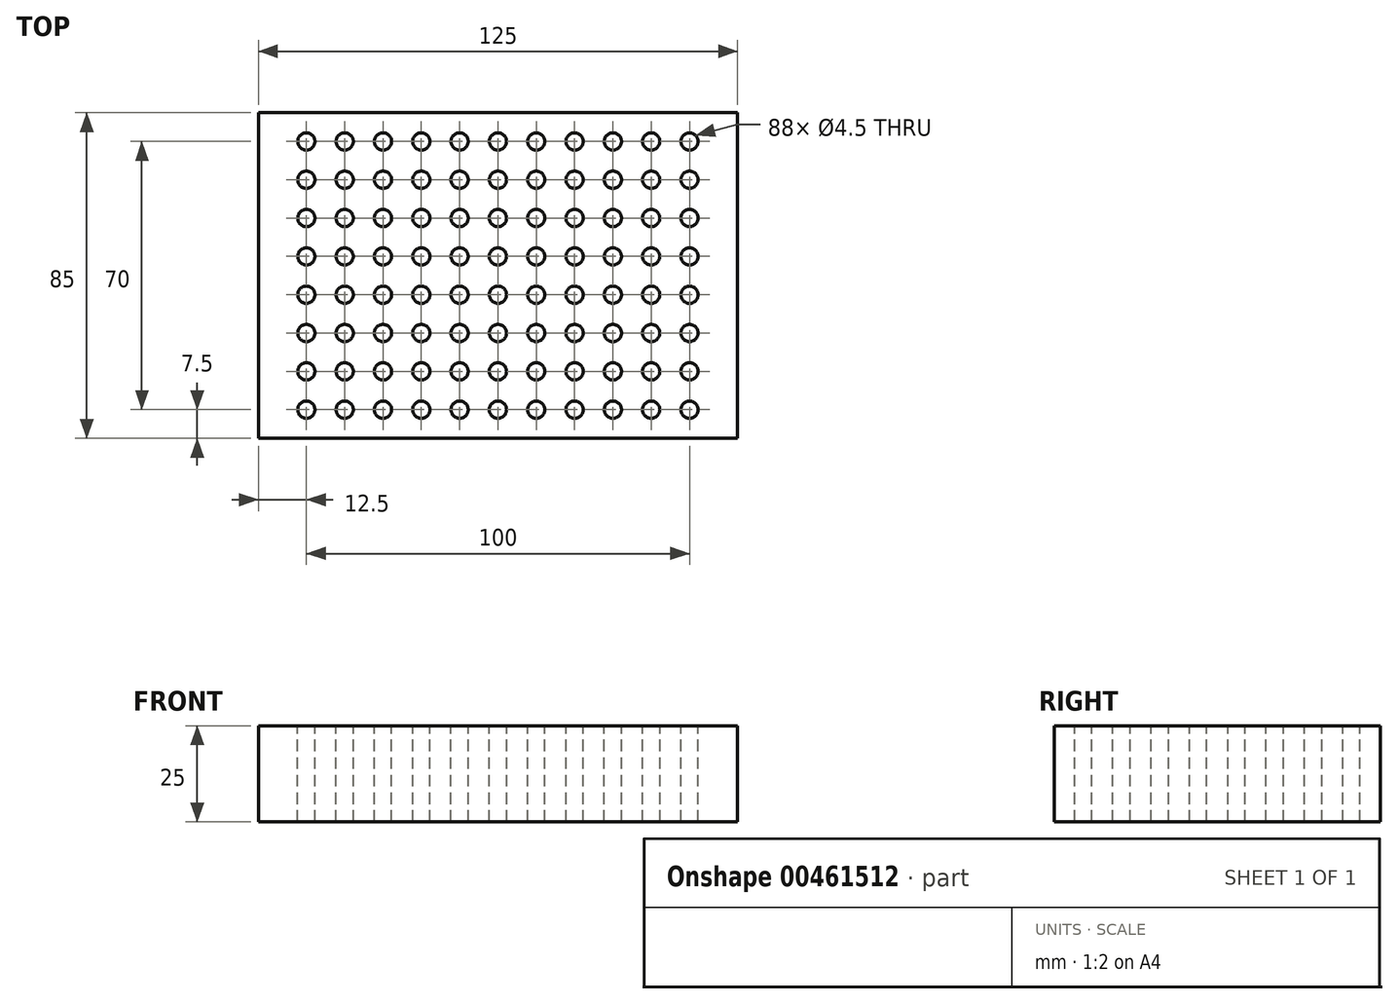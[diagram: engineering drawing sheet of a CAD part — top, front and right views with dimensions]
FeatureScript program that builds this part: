
annotation { "Feature Type Name" : "Feature", "Feature Type Description" : "" }
export const myFeature = defineFeature(function(context is Context, id is Id, definition is map)
    precondition{}
    {
        {
            var Q0;
            Q0=qCreatedBy(makeId("Top.planeOp"),FACE);
            var sketch = newSketch(context, id + "F0", { "sketchPlane" : qUnion([Q0])});
            skLineSegment(sketch, "E0.bottom", {"start": v(62.5, -42.5) * mm, "end": v(-62.5, -42.5) * mm});
            skLineSegment(sketch, "E0.top", {"start": v(62.5, 42.5) * mm, "end": v(-62.5, 42.5) * mm});
            skLineSegment(sketch, "E0.left", {"start": v(62.5, -42.5) * mm, "end": v(62.5, 42.5) * mm});
            skLineSegment(sketch, "E0.right", {"start": v(-62.5, -42.5) * mm, "end": v(-62.5, 42.5) * mm});
            skPoint(sketch, "E0.middle", {"position": v(0, 0) * mm});
            skSolve(sketch);
        }
        {
            var Q0;
            Q0 = qSketchRegion(id + "F0", true);
            extrude(context, id + "F1", {"entities" : qUnion([Q0]), "depth" : 25 * mm});
        }
        {
            var Q0;
            Q0=makeQuery(id+"F1.opExtrude","CAP_FACE",FACE,{"disambiguationData":[OSD([sQuery(id+"F0.wireOp",EDGE,"E0.bottom"),sQuery(id+"F0.wireOp",EDGE,"E0.top"),sQuery(id+"F0.wireOp",EDGE,"E0.left"),sQuery(id+"F0.wireOp",EDGE,"E0.right")])],"isStart":false});
            var sketch = newSketch(context, id + "F2", { "sketchPlane" : qUnion([Q0])});
            skCircle(sketch, "E1", {"center": v(-50, 35) * mm, "radius": 2.25 * mm});
            skCircle(sketch, "E2.0.1.0", {"center": v(-50, 25) * mm, "radius": 2.25 * mm});
            skCircle(sketch, "E2.0.2.0", {"center": v(-50, 15) * mm, "radius": 2.25 * mm});
            skCircle(sketch, "E2.0.3.0", {"center": v(-50, 5) * mm, "radius": 2.25 * mm});
            skCircle(sketch, "E2.0.4.0", {"center": v(-50, -5) * mm, "radius": 2.25 * mm});
            skCircle(sketch, "E2.0.5.0", {"center": v(-50, -15) * mm, "radius": 2.25 * mm});
            skCircle(sketch, "E2.0.6.0", {"center": v(-50, -25) * mm, "radius": 2.25 * mm});
            skCircle(sketch, "E2.0.7.0", {"center": v(-50, -35) * mm, "radius": 2.25 * mm});
            skCircle(sketch, "E2.1.0.0", {"center": v(-40, 35) * mm, "radius": 2.25 * mm});
            skCircle(sketch, "E2.1.1.0", {"center": v(-40, 25) * mm, "radius": 2.25 * mm});
            skCircle(sketch, "E2.1.2.0", {"center": v(-40, 15) * mm, "radius": 2.25 * mm});
            skCircle(sketch, "E2.1.3.0", {"center": v(-40, 5) * mm, "radius": 2.25 * mm});
            skCircle(sketch, "E2.1.4.0", {"center": v(-40, -5) * mm, "radius": 2.25 * mm});
            skCircle(sketch, "E2.1.5.0", {"center": v(-40, -15) * mm, "radius": 2.25 * mm});
            skCircle(sketch, "E2.1.6.0", {"center": v(-40, -25) * mm, "radius": 2.25 * mm});
            skCircle(sketch, "E2.1.7.0", {"center": v(-40, -35) * mm, "radius": 2.25 * mm});
            skCircle(sketch, "E2.2.0.0", {"center": v(-30, 35) * mm, "radius": 2.25 * mm});
            skCircle(sketch, "E2.2.1.0", {"center": v(-30, 25) * mm, "radius": 2.25 * mm});
            skCircle(sketch, "E2.2.2.0", {"center": v(-30, 15) * mm, "radius": 2.25 * mm});
            skCircle(sketch, "E2.2.3.0", {"center": v(-30, 5) * mm, "radius": 2.25 * mm});
            skCircle(sketch, "E2.2.4.0", {"center": v(-30, -5) * mm, "radius": 2.25 * mm});
            skCircle(sketch, "E2.2.5.0", {"center": v(-30, -15) * mm, "radius": 2.25 * mm});
            skCircle(sketch, "E2.2.6.0", {"center": v(-30, -25) * mm, "radius": 2.25 * mm});
            skCircle(sketch, "E2.2.7.0", {"center": v(-30, -35) * mm, "radius": 2.25 * mm});
            skCircle(sketch, "E2.3.0.0", {"center": v(-20, 35) * mm, "radius": 2.25 * mm});
            skCircle(sketch, "E2.3.1.0", {"center": v(-20, 25) * mm, "radius": 2.25 * mm});
            skCircle(sketch, "E2.3.2.0", {"center": v(-20, 15) * mm, "radius": 2.25 * mm});
            skCircle(sketch, "E2.3.3.0", {"center": v(-20, 5) * mm, "radius": 2.25 * mm});
            skCircle(sketch, "E2.3.4.0", {"center": v(-20, -5) * mm, "radius": 2.25 * mm});
            skCircle(sketch, "E2.3.5.0", {"center": v(-20, -15) * mm, "radius": 2.25 * mm});
            skCircle(sketch, "E2.3.6.0", {"center": v(-20, -25) * mm, "radius": 2.25 * mm});
            skCircle(sketch, "E2.3.7.0", {"center": v(-20, -35) * mm, "radius": 2.25 * mm});
            skCircle(sketch, "E2.4.0.0", {"center": v(-10, 35) * mm, "radius": 2.25 * mm});
            skCircle(sketch, "E2.4.1.0", {"center": v(-10, 25) * mm, "radius": 2.25 * mm});
            skCircle(sketch, "E2.4.2.0", {"center": v(-10, 15) * mm, "radius": 2.25 * mm});
            skCircle(sketch, "E2.4.3.0", {"center": v(-10, 5) * mm, "radius": 2.25 * mm});
            skCircle(sketch, "E2.4.4.0", {"center": v(-10, -5) * mm, "radius": 2.25 * mm});
            skCircle(sketch, "E2.4.5.0", {"center": v(-10, -15) * mm, "radius": 2.25 * mm});
            skCircle(sketch, "E2.4.6.0", {"center": v(-10, -25) * mm, "radius": 2.25 * mm});
            skCircle(sketch, "E2.4.7.0", {"center": v(-10, -35) * mm, "radius": 2.25 * mm});
            skCircle(sketch, "E2.5.0.0", {"center": v(0, 35) * mm, "radius": 2.25 * mm});
            skCircle(sketch, "E2.5.1.0", {"center": v(0, 25) * mm, "radius": 2.25 * mm});
            skCircle(sketch, "E2.5.2.0", {"center": v(0, 15) * mm, "radius": 2.25 * mm});
            skCircle(sketch, "E2.5.3.0", {"center": v(0, 5) * mm, "radius": 2.25 * mm});
            skCircle(sketch, "E2.5.4.0", {"center": v(0, -5) * mm, "radius": 2.25 * mm});
            skCircle(sketch, "E2.5.5.0", {"center": v(0, -15) * mm, "radius": 2.25 * mm});
            skCircle(sketch, "E2.5.6.0", {"center": v(0, -25) * mm, "radius": 2.25 * mm});
            skCircle(sketch, "E2.5.7.0", {"center": v(0, -35) * mm, "radius": 2.25 * mm});
            skCircle(sketch, "E2.6.0.0", {"center": v(10, 35) * mm, "radius": 2.25 * mm});
            skCircle(sketch, "E2.6.1.0", {"center": v(10, 25) * mm, "radius": 2.25 * mm});
            skCircle(sketch, "E2.6.2.0", {"center": v(10, 15) * mm, "radius": 2.25 * mm});
            skCircle(sketch, "E2.6.3.0", {"center": v(10, 5) * mm, "radius": 2.25 * mm});
            skCircle(sketch, "E2.6.4.0", {"center": v(10, -5) * mm, "radius": 2.25 * mm});
            skCircle(sketch, "E2.6.5.0", {"center": v(10, -15) * mm, "radius": 2.25 * mm});
            skCircle(sketch, "E2.6.6.0", {"center": v(10, -25) * mm, "radius": 2.25 * mm});
            skCircle(sketch, "E2.6.7.0", {"center": v(10, -35) * mm, "radius": 2.25 * mm});
            skCircle(sketch, "E2.7.0.0", {"center": v(20, 35) * mm, "radius": 2.25 * mm});
            skCircle(sketch, "E2.7.1.0", {"center": v(20, 25) * mm, "radius": 2.25 * mm});
            skCircle(sketch, "E2.7.2.0", {"center": v(20, 15) * mm, "radius": 2.25 * mm});
            skCircle(sketch, "E2.7.3.0", {"center": v(20, 5) * mm, "radius": 2.25 * mm});
            skCircle(sketch, "E2.7.4.0", {"center": v(20, -5) * mm, "radius": 2.25 * mm});
            skCircle(sketch, "E2.7.5.0", {"center": v(20, -15) * mm, "radius": 2.25 * mm});
            skCircle(sketch, "E2.7.6.0", {"center": v(20, -25) * mm, "radius": 2.25 * mm});
            skCircle(sketch, "E2.7.7.0", {"center": v(20, -35) * mm, "radius": 2.25 * mm});
            skCircle(sketch, "E2.8.0.0", {"center": v(30, 35) * mm, "radius": 2.25 * mm});
            skCircle(sketch, "E2.8.1.0", {"center": v(30, 25) * mm, "radius": 2.25 * mm});
            skCircle(sketch, "E2.8.2.0", {"center": v(30, 15) * mm, "radius": 2.25 * mm});
            skCircle(sketch, "E2.8.3.0", {"center": v(30, 5) * mm, "radius": 2.25 * mm});
            skCircle(sketch, "E2.8.4.0", {"center": v(30, -5) * mm, "radius": 2.25 * mm});
            skCircle(sketch, "E2.8.5.0", {"center": v(30, -15) * mm, "radius": 2.25 * mm});
            skCircle(sketch, "E2.8.6.0", {"center": v(30, -25) * mm, "radius": 2.25 * mm});
            skCircle(sketch, "E2.8.7.0", {"center": v(30, -35) * mm, "radius": 2.25 * mm});
            skCircle(sketch, "E2.9.0.0", {"center": v(40, 35) * mm, "radius": 2.25 * mm});
            skCircle(sketch, "E2.9.1.0", {"center": v(40, 25) * mm, "radius": 2.25 * mm});
            skCircle(sketch, "E2.9.2.0", {"center": v(40, 15) * mm, "radius": 2.25 * mm});
            skCircle(sketch, "E2.9.3.0", {"center": v(40, 5) * mm, "radius": 2.25 * mm});
            skCircle(sketch, "E2.9.4.0", {"center": v(40, -5) * mm, "radius": 2.25 * mm});
            skCircle(sketch, "E2.9.5.0", {"center": v(40, -15) * mm, "radius": 2.25 * mm});
            skCircle(sketch, "E2.9.6.0", {"center": v(40, -25) * mm, "radius": 2.25 * mm});
            skCircle(sketch, "E2.9.7.0", {"center": v(40, -35) * mm, "radius": 2.25 * mm});
            skCircle(sketch, "E2.10.0.0", {"center": v(50, 35) * mm, "radius": 2.25 * mm});
            skCircle(sketch, "E2.10.1.0", {"center": v(50, 25) * mm, "radius": 2.25 * mm});
            skCircle(sketch, "E2.10.2.0", {"center": v(50, 15) * mm, "radius": 2.25 * mm});
            skCircle(sketch, "E2.10.3.0", {"center": v(50, 5) * mm, "radius": 2.25 * mm});
            skCircle(sketch, "E2.10.4.0", {"center": v(50, -5) * mm, "radius": 2.25 * mm});
            skCircle(sketch, "E2.10.5.0", {"center": v(50, -15) * mm, "radius": 2.25 * mm});
            skCircle(sketch, "E2.10.6.0", {"center": v(50, -25) * mm, "radius": 2.25 * mm});
            skCircle(sketch, "E2.10.7.0", {"center": v(50, -35) * mm, "radius": 2.25 * mm});
            skLineSegment(sketch, "E2.direction1", {"start": v(-50, 35) * mm, "end": v(-40, 35) * mm, "construction": true});
            skLineSegment(sketch, "E2.direction2", {"start": v(-50, 35) * mm, "end": v(-50, 25) * mm, "construction": true});
            skSolve(sketch);
        }
        {
            var Q0;
            Q0 = qSketchRegion(id + "F2", true);
            extrude(context, id + "F3", {"entities" : qUnion([Q0]), "operationType" : NewBodyOperationType.REMOVE, "oppositeDirection" : true, "depth" : 25 * mm});
        }
    });
